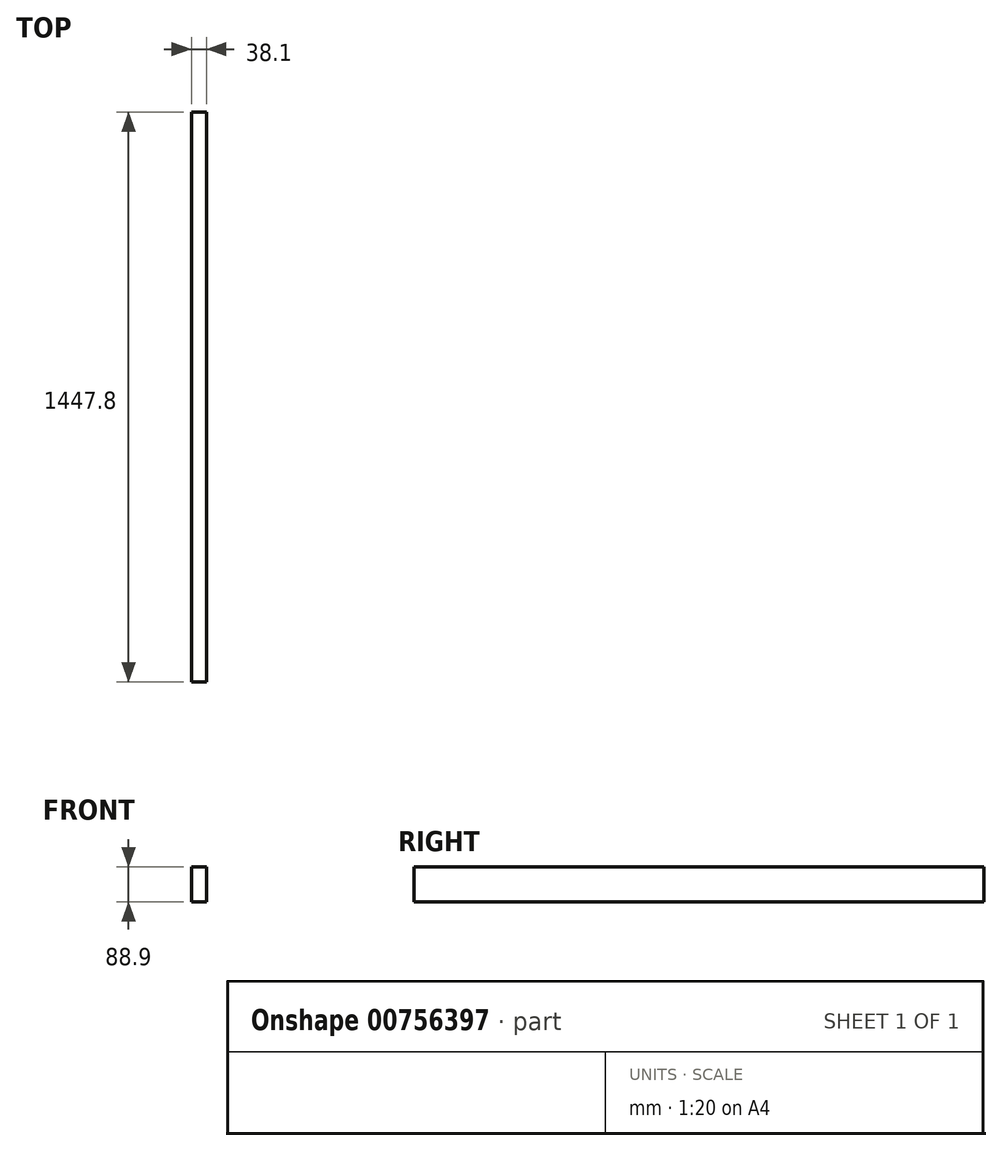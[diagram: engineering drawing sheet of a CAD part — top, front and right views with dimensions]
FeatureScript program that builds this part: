
annotation { "Feature Type Name" : "Feature", "Feature Type Description" : "" }
export const myFeature = defineFeature(function(context is Context, id is Id, definition is map)
    precondition{}
    {
        {
            var Q0;
            Q0=qCreatedBy(makeId("Front.planeOp"),FACE);
            var sketch = newSketch(context, id + "F0", { "sketchPlane" : qUnion([Q0])});
            skLineSegment(sketch, "E0.bottom", {"start": v(0, 88.9) * mm, "end": v(38.1, 88.9) * mm});
            skLineSegment(sketch, "E0.top", {"start": v(0, 0) * mm, "end": v(38.1, 0) * mm});
            skLineSegment(sketch, "E0.left", {"start": v(0, 88.9) * mm, "end": v(0, 0) * mm});
            skLineSegment(sketch, "E0.right", {"start": v(38.1, 88.9) * mm, "end": v(38.1, 0) * mm});
            skPoint(sketch, "E1.visualSharp", {"position": v(0, 88.9) * mm});
            skPoint(sketch, "E2.visualSharp", {"position": v(38.1, 88.9) * mm});
            skPoint(sketch, "E3.visualSharp", {"position": v(0, 0) * mm});
            skPoint(sketch, "E4.visualSharp", {"position": v(38.1, 0) * mm});
            skSolve(sketch);
        }
        {
            var Q0;
            Q0=makeQuery(id+"F0.imprint","IMPRINT",FACE,{"disambiguationData":[TD([[makeQuery(id+"F0.imprint","IMPRINT",EDGE,{"derivedFrom":sQuery(id+"F0.wireOp",EDGE,"E0.bottom")}),-1.0]])]});
            extrude(context, id + "F1", {"entities" : qUnion([Q0]), "depth" : 1524 * mm - 76.2 * mm, "offsetDistance" : 25.4 * mm});
        }
    });
